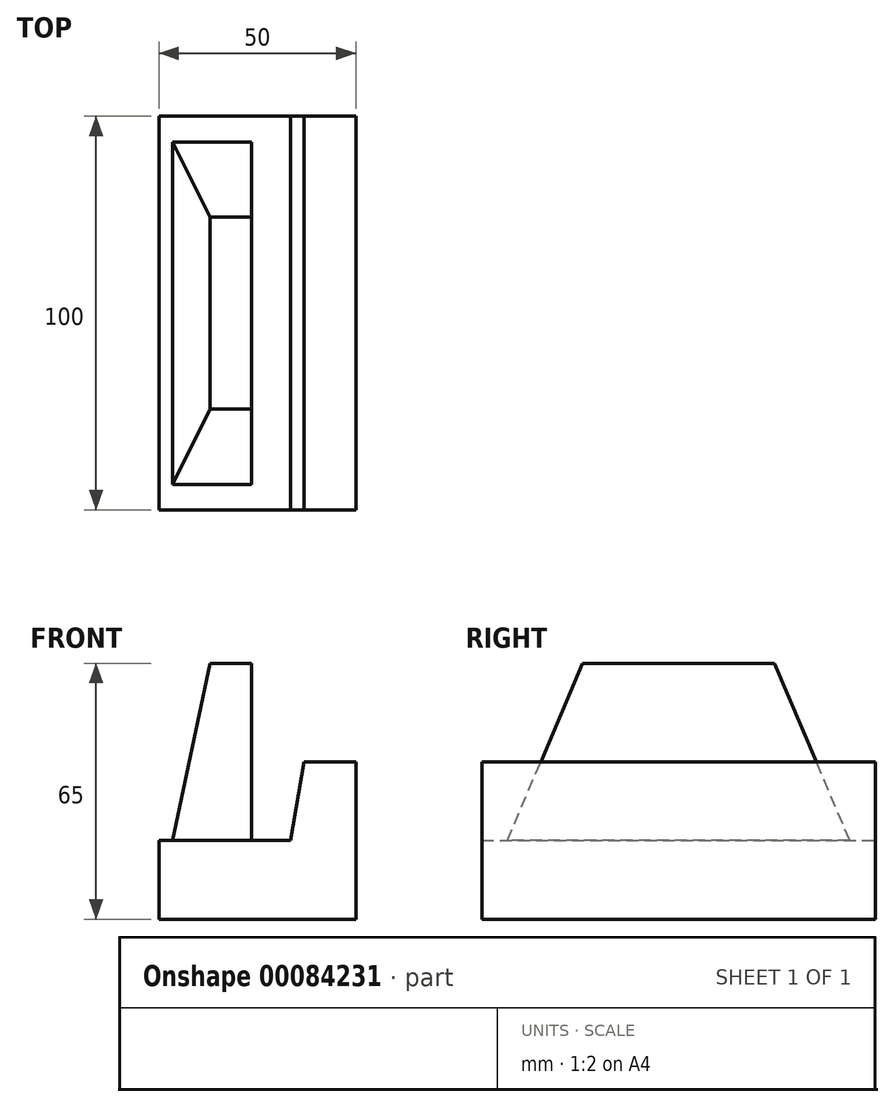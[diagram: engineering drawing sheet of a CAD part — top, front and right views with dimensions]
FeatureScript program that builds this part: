
annotation { "Feature Type Name" : "Feature", "Feature Type Description" : "" }
export const myFeature = defineFeature(function(context is Context, id is Id, definition is map)
    precondition{}
    {
        {
            var Q0;
            Q0=qCreatedBy(makeId("Front.planeOp"),FACE);
            var sketch = newSketch(context, id + "F0", { "sketchPlane" : qUnion([Q0])});
            skLineSegment(sketch, "E0", {"start": v(0, 0) * mm, "end": v(0, 40) * mm});
            skLineSegment(sketch, "E1", {"start": v(0, 40) * mm, "end": v(-13.2, 40) * mm});
            skLineSegment(sketch, "E2", {"start": v(-13.2, 40) * mm, "end": v(-16.55, 20) * mm});
            skLineSegment(sketch, "E3", {"start": v(-16.55, 20) * mm, "end": v(-50, 20) * mm});
            skLineSegment(sketch, "E4", {"start": v(-50, 20) * mm, "end": v(-50, 0) * mm});
            skLineSegment(sketch, "E5", {"start": v(-50, 0) * mm, "end": v(0, 0) * mm});
            skSolve(sketch);
        }
        {
            var Q0;
            Q0=makeQuery(id+"F0.imprint","IMPRINT",FACE,{"disambiguationData":[TD([[makeQuery(id+"F0.imprint","IMPRINT",EDGE,{"derivedFrom":sQuery(id+"F0.wireOp",EDGE,"E0")}),1.0]])]});
            extrude(context, id + "F1", {"entities" : qUnion([Q0]), "depth" : 100 * mm});
        }
        {
            var Q0;
            Q0=makeQuery(id+"F1.opExtrude","SWEPT_FACE",FACE,{"disambiguationData":[OSD([sQuery(id+"F0.wireOp",EDGE,"E3")])]});
            var sketch = newSketch(context, id + "F2", { "sketchPlane" : qUnion([Q0])});
            skLineSegment(sketch, "E6.0", {"start": v(-16.55, -100) * mm, "end": v(-16.55, 0) * mm});
            skLineSegment(sketch, "E6.1", {"start": v(-16.55, 0) * mm, "end": v(-50, 0) * mm});
            skLineSegment(sketch, "E6.2", {"start": v(-50, -100) * mm, "end": v(-50, 0) * mm});
            skLineSegment(sketch, "E6.3", {"start": v(-16.55, -100) * mm, "end": v(-50, -100) * mm});
            skLineSegment(sketch, "E7", {"start": v(-16.55, -50) * mm, "end": v(-50, -50) * mm, "construction": true});
            skLineSegment(sketch, "E8.bottom", {"start": v(-26.55, -6.5) * mm, "end": v(-46.55, -6.5) * mm});
            skLineSegment(sketch, "E8.top", {"start": v(-26.55, -93.5) * mm, "end": v(-46.55, -93.5) * mm});
            skLineSegment(sketch, "E8.left", {"start": v(-26.55, -6.5) * mm, "end": v(-26.55, -93.5) * mm});
            skLineSegment(sketch, "E8.right", {"start": v(-46.55, -6.5) * mm, "end": v(-46.55, -93.5) * mm});
            skPoint(sketch, "E8.middle", {"position": v(-36.55, -50) * mm});
            skSolve(sketch);
        }
        {
            var Q0;
            Q0=makeQuery(id+"F2.imprint","IMPRINT",FACE,{"disambiguationData":[TD([[makeQuery(id+"F2.imprint","IMPRINT",EDGE,{"derivedFrom":sQuery(id+"F2.wireOp",EDGE,"E6.0")}),1.0]])]});
            cPlane(context, id + "F3", {"entities" : qUnion([Q0]), "cplaneType" : CPlaneType.OFFSET, "offset" : 45 * mm, "width" : 150 * mm, "height" : 150 * mm});
        }
        {
            var Q0;
            Q0=qCreatedBy(id+"F3.planeOp",FACE);
            var sketch = newSketch(context, id + "F4", { "sketchPlane" : qUnion([Q0])});
            skLineSegment(sketch, "E9.0", {"start": v(-16.55, -100) * mm, "end": v(-16.55, 0) * mm, "construction": true});
            skLineSegment(sketch, "E9.1", {"start": v(-16.55, -50) * mm, "end": v(-50, -50) * mm, "construction": true});
            skLineSegment(sketch, "E9.2", {"start": v(-16.55, 0) * mm, "end": v(-50, 0) * mm, "construction": true});
            skLineSegment(sketch, "E9.3", {"start": v(-50, -100) * mm, "end": v(-50, 0) * mm, "construction": true});
            skLineSegment(sketch, "E9.4", {"start": v(-16.55, -100) * mm, "end": v(-50, -100) * mm, "construction": true});
            skLineSegment(sketch, "E10.0", {"start": v(-26.55, -6.5) * mm, "end": v(-26.55, -93.5) * mm, "construction": true});
            skLineSegment(sketch, "E10.1", {"start": v(-26.55, -6.5) * mm, "end": v(-46.55, -6.5) * mm, "construction": true});
            skLineSegment(sketch, "E10.2", {"start": v(-46.55, -6.5) * mm, "end": v(-46.55, -93.5) * mm, "construction": true});
            skLineSegment(sketch, "E10.3", {"start": v(-26.55, -93.5) * mm, "end": v(-46.55, -93.5) * mm, "construction": true});
            skLineSegment(sketch, "E11.bottom", {"start": v(-26.55, -25.6) * mm, "end": v(-37.05, -25.6) * mm});
            skLineSegment(sketch, "E11.top", {"start": v(-26.55, -74.4) * mm, "end": v(-37.05, -74.4) * mm});
            skLineSegment(sketch, "E11.left", {"start": v(-26.55, -25.6) * mm, "end": v(-26.55, -74.4) * mm});
            skLineSegment(sketch, "E11.right", {"start": v(-37.05, -25.6) * mm, "end": v(-37.05, -74.4) * mm});
            skPoint(sketch, "E11.middle", {"position": v(-31.8, -50) * mm});
            skSolve(sketch);
        }
        {
            var Q1;
            Q1=makeQuery(id+"F2.imprint","IMPRINT",FACE,{"disambiguationData":[TD([[makeQuery(id+"F2.imprint","IMPRINT",EDGE,{"derivedFrom":sQuery(id+"F2.wireOp",EDGE,"E8.bottom")}),1.0]])]});
            var Q2;
            Q2=makeQuery(id+"F4.imprint","IMPRINT",FACE,{"disambiguationData":[TD([[makeQuery(id+"F4.imprint","IMPRINT",EDGE,{"derivedFrom":sQuery(id+"F4.wireOp",EDGE,"E11.bottom")}),1.0]])]});
            loft(context, id + "F5", {"operationType" : NewBodyOperationType.ADD, "sheetProfilesArray" : [{ "sheetProfileEntities" : qUnion([Q1]) }, { "sheetProfileEntities" : qUnion([Q2]) }]});
        }
    });
